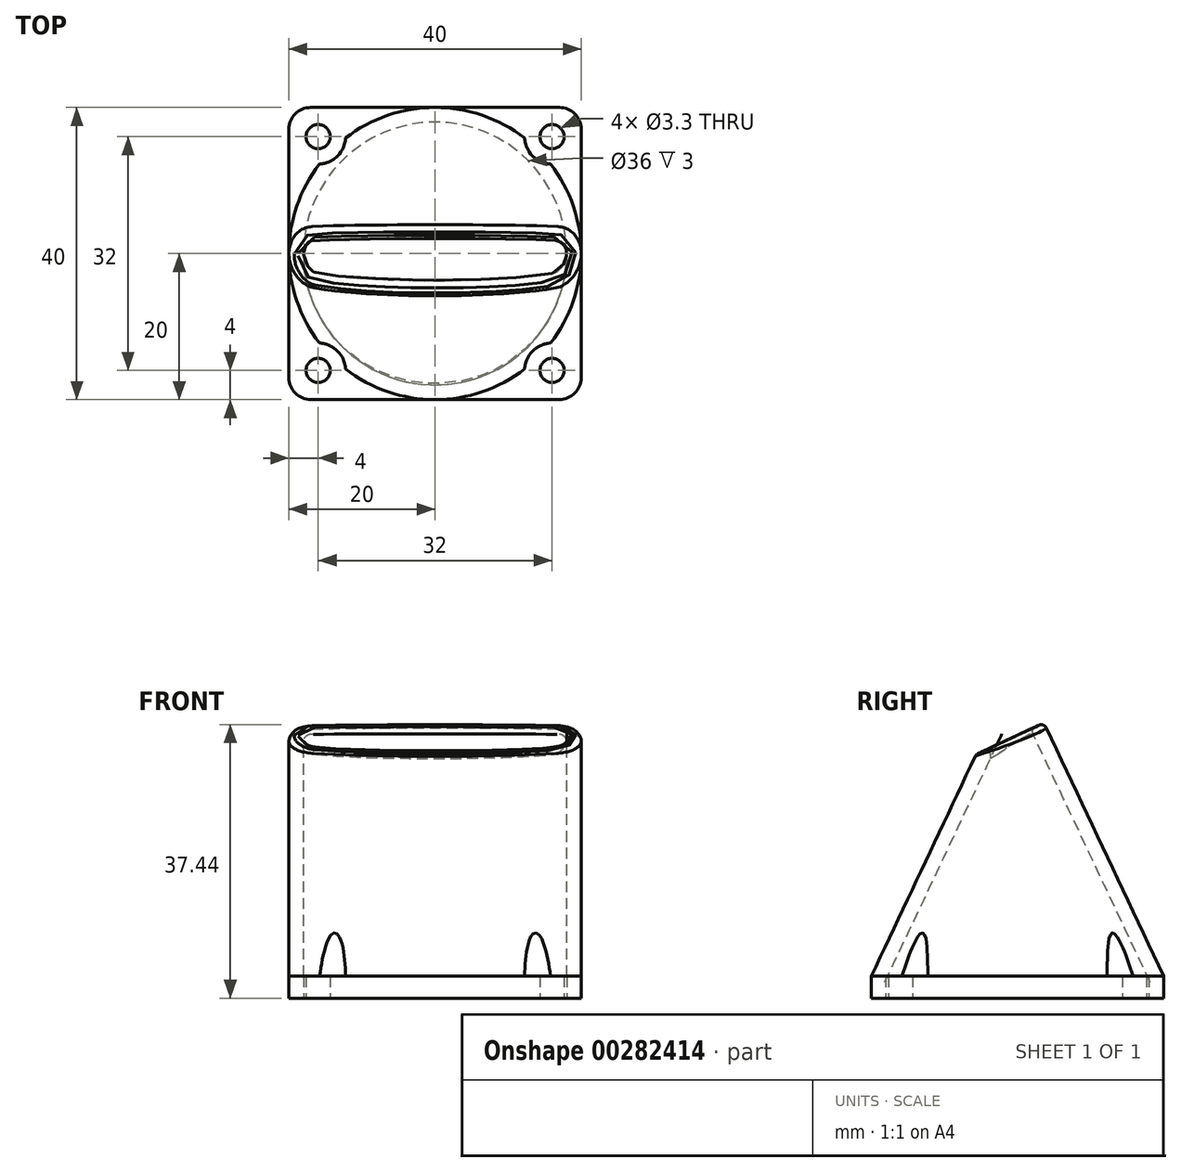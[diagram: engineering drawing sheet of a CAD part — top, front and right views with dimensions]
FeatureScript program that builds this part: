
annotation { "Feature Type Name" : "Feature", "Feature Type Description" : "" }
export const myFeature = defineFeature(function(context is Context, id is Id, definition is map)
    precondition{}
    {
        {
            var Q0;
            Q0=qCreatedBy(makeId("Top.planeOp"),FACE);
            var sketch = newSketch(context, id + "F0", { "sketchPlane" : qUnion([Q0])});
            skLineSegment(sketch, "E0.bottom", {"start": v(3, 0) * mm, "end": v(37, 0) * mm});
            skLineSegment(sketch, "E0.top", {"start": v(3, -40) * mm, "end": v(37, -40) * mm});
            skLineSegment(sketch, "E0.left", {"start": v(0, -3) * mm, "end": v(0, -37) * mm});
            skLineSegment(sketch, "E0.right", {"start": v(40, -3) * mm, "end": v(40, -37) * mm});
            skLineSegment(sketch, "E1", {"start": v(0, 0) * mm, "end": v(40, -40) * mm, "construction": true});
            skLineSegment(sketch, "E2", {"start": v(0, -40) * mm, "end": v(40, 0) * mm, "construction": true});
            skLineSegment(sketch, "E3", {"start": v(20, 0) * mm, "end": v(20, -40) * mm, "construction": true});
            skCircle(sketch, "E4", {"center": v(20, -20) * mm, "radius": 18 * mm});
            skCircle(sketch, "E5", {"center": v(4, -4) * mm, "radius": 1.65 * mm});
            skCircle(sketch, "E6", {"center": v(36, -4) * mm, "radius": 1.65 * mm});
            skCircle(sketch, "E7", {"center": v(36, -36) * mm, "radius": 1.65 * mm});
            skCircle(sketch, "E8", {"center": v(4, -36) * mm, "radius": 1.65 * mm});
            skPoint(sketch, "E9.visualSharp", {"position": v(0, -40) * mm});
            skArc(sketch, "E9.filletArc", {"start": v(0, -37) * mm, "mid": v(0.88, -39.12) * mm, "end": v(3, -40) * mm});
            skPoint(sketch, "E10.visualSharp", {"position": v(40, -40) * mm});
            skArc(sketch, "E10.filletArc", {"start": v(37, -40) * mm, "mid": v(39.12, -39.12) * mm, "end": v(40, -37) * mm});
            skPoint(sketch, "E11.visualSharp", {"position": v(40, 0) * mm});
            skArc(sketch, "E11.filletArc", {"start": v(40, -3) * mm, "mid": v(39.12, -0.88) * mm, "end": v(37, 0) * mm});
            skPoint(sketch, "E12.visualSharp", {"position": v(0, 0) * mm});
            skArc(sketch, "E12.filletArc", {"start": v(3, 0) * mm, "mid": v(0.88, -0.88) * mm, "end": v(0, -3) * mm});
            skSolve(sketch);
        }
        {
            var Q0;
            Q0=qSketchRegion(id+"F0",true);
            extrude(context, id + "F1", {"entities" : qUnion([Q0]), "depth" : 3 * mm});
        }
        {
            var Q0;
            Q0=makeQuery(id+"F1.opExtrude","CAP_FACE",FACE,{"disambiguationData":[OSD([sQuery(id+"F0.wireOp",EDGE,"E0.bottom"),sQuery(id+"F0.wireOp",EDGE,"E0.top"),sQuery(id+"F0.wireOp",EDGE,"E0.left"),sQuery(id+"F0.wireOp",EDGE,"E0.right"),sQuery(id+"F0.wireOp",EDGE,"E4"),sQuery(id+"F0.wireOp",EDGE,"E5"),sQuery(id+"F0.wireOp",EDGE,"E6"),sQuery(id+"F0.wireOp",EDGE,"E7"),sQuery(id+"F0.wireOp",EDGE,"E8"),sQuery(id+"F0.wireOp",EDGE,"E9.filletArc"),sQuery(id+"F0.wireOp",EDGE,"E10.filletArc"),sQuery(id+"F0.wireOp",EDGE,"E11.filletArc"),sQuery(id+"F0.wireOp",EDGE,"E12.filletArc")])],"isStart":false});
            var sketch = newSketch(context, id + "F2", { "sketchPlane" : qUnion([Q0])});
            skLineSegment(sketch, "E13", {"start": v(0, 0) * mm, "end": v(20, -20) * mm, "construction": true});
            skLineSegment(sketch, "E14", {"start": v(4, -36) * mm, "end": v(36, -4) * mm, "construction": true});
            skLineSegment(sketch, "E15", {"start": v(20, -20) * mm, "end": v(36, -36) * mm, "construction": true});
            skArc(sketch, "E16", {"start": v(5.86, -5.86) * mm, "mid": v(1.52, -12.35) * mm, "end": v(0, -20) * mm});
            skArc(sketch, "E17", {"start": v(5.86, -34.14) * mm, "mid": v(20, -40) * mm, "end": v(34.14, -34.14) * mm});
            skArc(sketch, "E18", {"start": v(34.14, -5.86) * mm, "mid": v(20, 0) * mm, "end": v(5.86, -5.86) * mm});
            skArc(sketch, "E19", {"start": v(34.14, -34.14) * mm, "mid": v(38.48, -27.65) * mm, "end": v(40, -20) * mm});
            skLineSegment(sketch, "E20", {"start": v(0, -20) * mm, "end": v(40, -20) * mm, "construction": true});
            skArc(sketch, "E21", {"start": v(0, -20) * mm, "mid": v(1.52, -27.65) * mm, "end": v(5.86, -34.14) * mm});
            skArc(sketch, "E22", {"start": v(40, -20) * mm, "mid": v(38.48, -12.35) * mm, "end": v(34.14, -5.86) * mm});
            skSolve(sketch);
        }
        {
            var Q0;
            Q0=makeQuery(id+"F2.imprint","IMPRINT",FACE,{"disambiguationData":[TD([[makeQuery(id+"F2.imprint","IMPRINT",EDGE,{"derivedFrom":makeQuery(id+"F1.opExtrude","CAP_EDGE",EDGE,{"disambiguationData":[OSD([sQuery(id+"F0.wireOp",EDGE,"E6")])],"isStart":false})}),-1.0]])]});
            cPlane(context, id + "F3", {"entities" : qUnion([Q0]), "cplaneType" : CPlaneType.OFFSET, "offset" : 36 * mm, "width" : 150 * mm, "height" : 150 * mm});
        }
        {
            var Q0;
            Q0=qCreatedBy(id+"F3.planeOp",FACE);
            var sketch = newSketch(context, id + "F4", { "sketchPlane" : qUnion([Q0])});
            skLineSegment(sketch, "E23", {"start": v(20, -20) * mm, "end": v(40, -20) * mm, "construction": true});
            skArc(sketch, "E24", {"start": v(3, -17) * mm, "mid": v(0.88, -17.88) * mm, "end": v(0, -20) * mm});
            skArc(sketch, "E25", {"start": v(37, -23) * mm, "mid": v(39.12, -22.12) * mm, "end": v(40, -20) * mm});
            skLineSegment(sketch, "E26", {"start": v(3, -17) * mm, "end": v(37, -17) * mm});
            skLineSegment(sketch, "E27", {"start": v(3, -23) * mm, "end": v(37, -23) * mm});
            skLineSegment(sketch, "E28", {"start": v(0, 0) * mm, "end": v(20, -20) * mm, "construction": true});
            skLineSegment(sketch, "E29", {"start": v(0, -20) * mm, "end": v(20, -20) * mm, "construction": true});
            skArc(sketch, "E30", {"start": v(0, -20) * mm, "mid": v(0.88, -22.12) * mm, "end": v(3, -23) * mm});
            skArc(sketch, "E31", {"start": v(40, -20) * mm, "mid": v(39.12, -17.88) * mm, "end": v(37, -17) * mm});
            skSolve(sketch);
        }
        {
            var Q0;
            Q0=makeQuery(id+"F1.opExtrude","SWEPT_FACE",FACE,{"disambiguationData":[OSD([sQuery(id+"F0.wireOp",EDGE,"E0.top")])]});
            cPlane(context, id + "F5", {"entities" : qUnion([Q0]), "cplaneType" : CPlaneType.OFFSET, "offset" : 20 * mm, "oppositeDirection" : true, "width" : 150 * mm, "height" : 150 * mm});
        }
        {
            var Q0;
            Q0=qCreatedBy(id+"F5.planeOp",FACE);
            var sketch = newSketch(context, id + "F6", { "sketchPlane" : qUnion([Q0])});
            skLineSegment(sketch, "E32", {"start": v(0, 0) * mm, "end": v(0, 3) * mm, "construction": true});
            skLineSegment(sketch, "E33", {"start": v(0, 3) * mm, "end": v(0, 39) * mm});
            skLineSegment(sketch, "E34", {"start": v(0, 0) * mm, "end": v(40, 0) * mm, "construction": true});
            skLineSegment(sketch, "E35", {"start": v(40, 0) * mm, "end": v(40, 3) * mm, "construction": true});
            skLineSegment(sketch, "E36", {"start": v(40, 3) * mm, "end": v(40, 39) * mm});
            skSolve(sketch);
        }
        {
            var Q0;
            Q0=makeQuery(id+"F1.opExtrude","SWEPT_FACE",FACE,{"disambiguationData":[OSD([sQuery(id+"F0.wireOp",EDGE,"E0.right")])]});
            cPlane(context, id + "F7", {"entities" : qUnion([Q0]), "cplaneType" : CPlaneType.OFFSET, "offset" : 20 * mm, "oppositeDirection" : true, "width" : 150 * mm, "height" : 150 * mm});
        }
        {
            var Q0;
            Q0=qCreatedBy(id+"F7.planeOp",FACE);
            var sketch = newSketch(context, id + "F8", { "sketchPlane" : qUnion([Q0])});
            skLineSegment(sketch, "E37", {"start": v(0, 0) * mm, "end": v(0, 3) * mm, "construction": true});
            skLineSegment(sketch, "E38", {"start": v(0, 3) * mm, "end": v(-40, 3) * mm, "construction": true});
            skLineSegment(sketch, "E39", {"start": v(0, 3) * mm, "end": v(0, 39) * mm, "construction": true});
            skLineSegment(sketch, "E40", {"start": v(0, 39) * mm, "end": v(-17, 39) * mm, "construction": true});
            skLineSegment(sketch, "E41", {"start": v(-17, 39) * mm, "end": v(-23, 39) * mm, "construction": true});
            skLineSegment(sketch, "E42", {"start": v(-23, 39) * mm, "end": v(-23, 42) * mm, "construction": true});
            skLineSegment(sketch, "E43", {"start": v(-40, 3) * mm, "end": v(-40, 0) * mm, "construction": true});
            skLineSegment(sketch, "E44", {"start": v(-23, 39) * mm, "end": v(-40, 3) * mm});
            skLineSegment(sketch, "E45", {"start": v(-17, 39) * mm, "end": v(0, 3) * mm});
            skSolve(sketch);
        }
        {
            var Q1;
            Q1=qSketchRegion(id+"F2",true);
            var Q2;
            Q2=qSketchRegion(id+"F4",true);
            var Q3;
            Q3=sQuery(id+"F6.wireOp",EDGE,"E36");
            var Q4;
            Q4=sQuery(id+"F6.wireOp",EDGE,"E33");
            var Q5;
            Q5=sQuery(id+"F8.wireOp",EDGE,"E44");
            var Q6;
            Q6=sQuery(id+"F8.wireOp",EDGE,"E45");
            loft(context, id + "F9", {"addGuides" : true, "sheetProfilesArray" : [{ "sheetProfileEntities" : qUnion([Q1]) }, { "sheetProfileEntities" : qUnion([Q2]) }], "guidesArray" : [{ "guideEntities" : qUnion([Q3]), "guideDerivativeType" : LoftGuideDerivativeType.DEFAULT, "guideDerivativeMagnitude" : 1 }, { "guideEntities" : qUnion([Q4]), "guideDerivativeType" : LoftGuideDerivativeType.DEFAULT, "guideDerivativeMagnitude" : 1 }, { "guideEntities" : qUnion([Q5]), "guideDerivativeType" : LoftGuideDerivativeType.DEFAULT, "guideDerivativeMagnitude" : 1 }, { "guideEntities" : qUnion([Q6]), "guideDerivativeType" : LoftGuideDerivativeType.DEFAULT, "guideDerivativeMagnitude" : 1 }]});
        }
        {
            var Q0;
            Q0=makeQuery(id+"F9.opLoft","CAP_FACE",FACE,{"disambiguationData":[OSD([makeQuery(id+"F4.imprint","IMPRINT",FACE,{"disambiguationData":[TD([[makeQuery(id+"F4.imprint","IMPRINT",EDGE,{"derivedFrom":sQuery(id+"F4.wireOp",EDGE,"E24")}),1.0]])]})])],"isStart":true});
            var Q1;
            {var subQ7=sQuery(id+"F2.wireOp",EDGE,"E16");Q1=makeQuery(id+"F9.opLoft","CAP_FACE",FACE,{"disambiguationData":[OSD([makeQuery(id+"F2.imprint","IMPRINT",FACE,{"disambiguationData":[TD([[makeQuery(id+"F2.imprint","IMPRINT",EDGE,{"derivedFrom":subQ7}),1.0]])]})])],"isStart":true});}
            shell(context, id + "F10", {"entities" : qUnion([Q0, Q1]), "thickness" : 2 * mm});
        }
        {
            var Q0;
            Q0=makeQuery(id+"F1.opExtrude","SWEPT_BODY",BODY,{"disambiguationData":[OSD([sQuery(id+"F0.wireOp",EDGE,"E0.bottom"),sQuery(id+"F0.wireOp",EDGE,"E0.top"),sQuery(id+"F0.wireOp",EDGE,"E0.left"),sQuery(id+"F0.wireOp",EDGE,"E0.right"),sQuery(id+"F0.wireOp",EDGE,"E4"),sQuery(id+"F0.wireOp",EDGE,"E5"),sQuery(id+"F0.wireOp",EDGE,"E6"),sQuery(id+"F0.wireOp",EDGE,"E7"),sQuery(id+"F0.wireOp",EDGE,"E8"),sQuery(id+"F0.wireOp",EDGE,"E9.filletArc"),sQuery(id+"F0.wireOp",EDGE,"E10.filletArc"),sQuery(id+"F0.wireOp",EDGE,"E11.filletArc"),sQuery(id+"F0.wireOp",EDGE,"E12.filletArc")])]});
            var Q1;
            Q1=makeQuery(id+"F9.opLoft","SWEPT_BODY",BODY,{"disambiguationData":[OSD([makeQuery(id+"F2.imprint","IMPRINT",FACE,{"disambiguationData":[TD([[makeQuery(id+"F2.imprint","IMPRINT",EDGE,{"derivedFrom":makeQuery(id+"F1.opExtrude","CAP_EDGE",EDGE,{"disambiguationData":[OSD([sQuery(id+"F0.wireOp",EDGE,"E4")])],"isStart":false})}),1.0]])]}),makeQuery(id+"F4.imprint","IMPRINT",FACE,{"disambiguationData":[TD([[makeQuery(id+"F4.imprint","IMPRINT",EDGE,{"derivedFrom":sQuery(id+"F4.wireOp",EDGE,"E24")}),1.0]])]}),sQuery(id+"F6.wireOp",EDGE,"E33"),sQuery(id+"F6.wireOp",EDGE,"E36")])]});
            booleanBodies(context, id + "F11", {"operationType" : BooleanOperationType.UNION, "tools" : qUnion([Q0, Q1])});
        }
        {
            var Q0;
            Q0=qCreatedBy(makeId("Right.planeOp"),FACE);
            var sketch = newSketch(context, id + "F12", { "sketchPlane" : qUnion([Q0])});
            skLineSegment(sketch, "E46", {"start": v(0, 0) * mm, "end": v(-20, 0) * mm, "construction": true});
            skLineSegment(sketch, "E47", {"start": v(-20, 0) * mm, "end": v(-20, 36) * mm, "construction": true});
            skLineSegment(sketch, "E48", {"start": v(-20, 36) * mm, "end": v(-1.87, 44.45) * mm});
            skLineSegment(sketch, "E49", {"start": v(-1.87, 44.45) * mm, "end": v(-6.95, 55.33) * mm});
            skLineSegment(sketch, "E50", {"start": v(-6.95, 55.33) * mm, "end": v(-43.2, 38.42) * mm});
            skLineSegment(sketch, "E51", {"start": v(-43.2, 38.42) * mm, "end": v(-38.13, 27.55) * mm});
            skLineSegment(sketch, "E52", {"start": v(-38.13, 27.55) * mm, "end": v(-20, 36) * mm});
            skSolve(sketch);
        }
        {
            var Q0;
            Q0=qSketchRegion(id+"F12",true);
            extrude(context, id + "F13", {"entities" : qUnion([Q0]), "operationType" : NewBodyOperationType.REMOVE, "endBound" : BoundingType.THROUGH_ALL, "depth" : 25 * mm});
        }
        {
            var Q0;
            Q0=makeQuery(id+"F13.boolean.opBoolean","INTERSECT",EDGE,{"derivedFrom":[makeQuery(id+"F10.opShell","OFFSET_FACE",FACE,{"disambiguationData":[OSD([sQuery(id+"F2.wireOp",EDGE,"E16"),sQuery(id+"F2.wireOp",EDGE,"E17"),sQuery(id+"F2.wireOp",EDGE,"E21"),sQuery(id+"F4.wireOp",EDGE,"E30"),sQuery(id+"F6.wireOp",EDGE,"E33")])]}),makeQuery(id+"F13.opExtrude","SWEPT_FACE",FACE,{"disambiguationData":[OSD([sQuery(id+"F12.wireOp",EDGE,"E48"),sQuery(id+"F12.wireOp",EDGE,"E52")])]})]});
            var Q1;
            Q1=makeQuery(id+"F13.boolean.opBoolean","INTERSECT",EDGE,{"derivedFrom":[makeQuery(id+"F9.opLoft","SWEPT_FACE",FACE,{"disambiguationData":[OSD([sQuery(id+"F2.wireOp",EDGE,"E16"),sQuery(id+"F2.wireOp",EDGE,"E17"),sQuery(id+"F2.wireOp",EDGE,"E21"),sQuery(id+"F4.wireOp",EDGE,"E30"),sQuery(id+"F6.wireOp",EDGE,"E33")])]}),makeQuery(id+"F13.opExtrude","SWEPT_FACE",FACE,{"disambiguationData":[OSD([sQuery(id+"F12.wireOp",EDGE,"E48"),sQuery(id+"F12.wireOp",EDGE,"E52")])]})]});
            fillet(context, id + "F14", {"entities" : qUnion([Q0, Q1]), "radius" : 0.75 * mm, "tangentPropagation" : true, "allowEdgeOverflow" : false});
        }
        {
            var Q0;
            {var subQ0=sQuery(id+"F0.wireOp",EDGE,"E0.right");var subQ1=sQuery(id+"F0.wireOp",EDGE,"E10.filletArc");var subQ2=sQuery(id+"F0.wireOp",EDGE,"E7");var subQ3=sQuery(id+"F0.wireOp",EDGE,"E0.top");var subQ4=makeQuery(id+"F1.opExtrude","CAP_FACE",FACE,{"disambiguationData":[OSD([sQuery(id+"F0.wireOp",EDGE,"E0.bottom"),subQ3,sQuery(id+"F0.wireOp",EDGE,"E0.left"),subQ0,sQuery(id+"F0.wireOp",EDGE,"E4"),sQuery(id+"F0.wireOp",EDGE,"E5"),sQuery(id+"F0.wireOp",EDGE,"E6"),subQ2,sQuery(id+"F0.wireOp",EDGE,"E8"),sQuery(id+"F0.wireOp",EDGE,"E9.filletArc"),subQ1,sQuery(id+"F0.wireOp",EDGE,"E11.filletArc"),sQuery(id+"F0.wireOp",EDGE,"E12.filletArc")])],"isStart":false});Q0=makeQuery(id+"F11.opBoolean","SPLIT",FACE,{"disambiguationData":[TD([makeQuery(id+"F1.opExtrude","SWEPT_FACE",FACE,{"disambiguationData":[OSD([subQ2])]})])],"derivedFrom":subQ4});}
            var sketch = newSketch(context, id + "F15", { "sketchPlane" : qUnion([Q0])});
            skCircle(sketch, "E53", {"center": v(36, -36) * mm, "radius": 3.75 * mm});
            skLineSegment(sketch, "E54.bottom", {"start": v(36, -36) * mm, "end": v(4, -36) * mm, "construction": true});
            skLineSegment(sketch, "E54.top", {"start": v(36, -4) * mm, "end": v(4, -4) * mm, "construction": true});
            skLineSegment(sketch, "E54.left", {"start": v(36, -36) * mm, "end": v(36, -4) * mm, "construction": true});
            skLineSegment(sketch, "E54.right", {"start": v(4, -36) * mm, "end": v(4, -4) * mm, "construction": true});
            skCircle(sketch, "E55", {"center": v(4, -36) * mm, "radius": 3.75 * mm});
            skCircle(sketch, "E56", {"center": v(4, -4) * mm, "radius": 3.75 * mm});
            skCircle(sketch, "E57", {"center": v(36, -4) * mm, "radius": 3.75 * mm});
            skSolve(sketch);
        }
        {
            var Q0;
            Q0=qSketchRegion(id+"F15",true);
            extrude(context, id + "F16", {"entities" : qUnion([Q0]), "operationType" : NewBodyOperationType.REMOVE, "depth" : 25 * mm});
        }
    });
